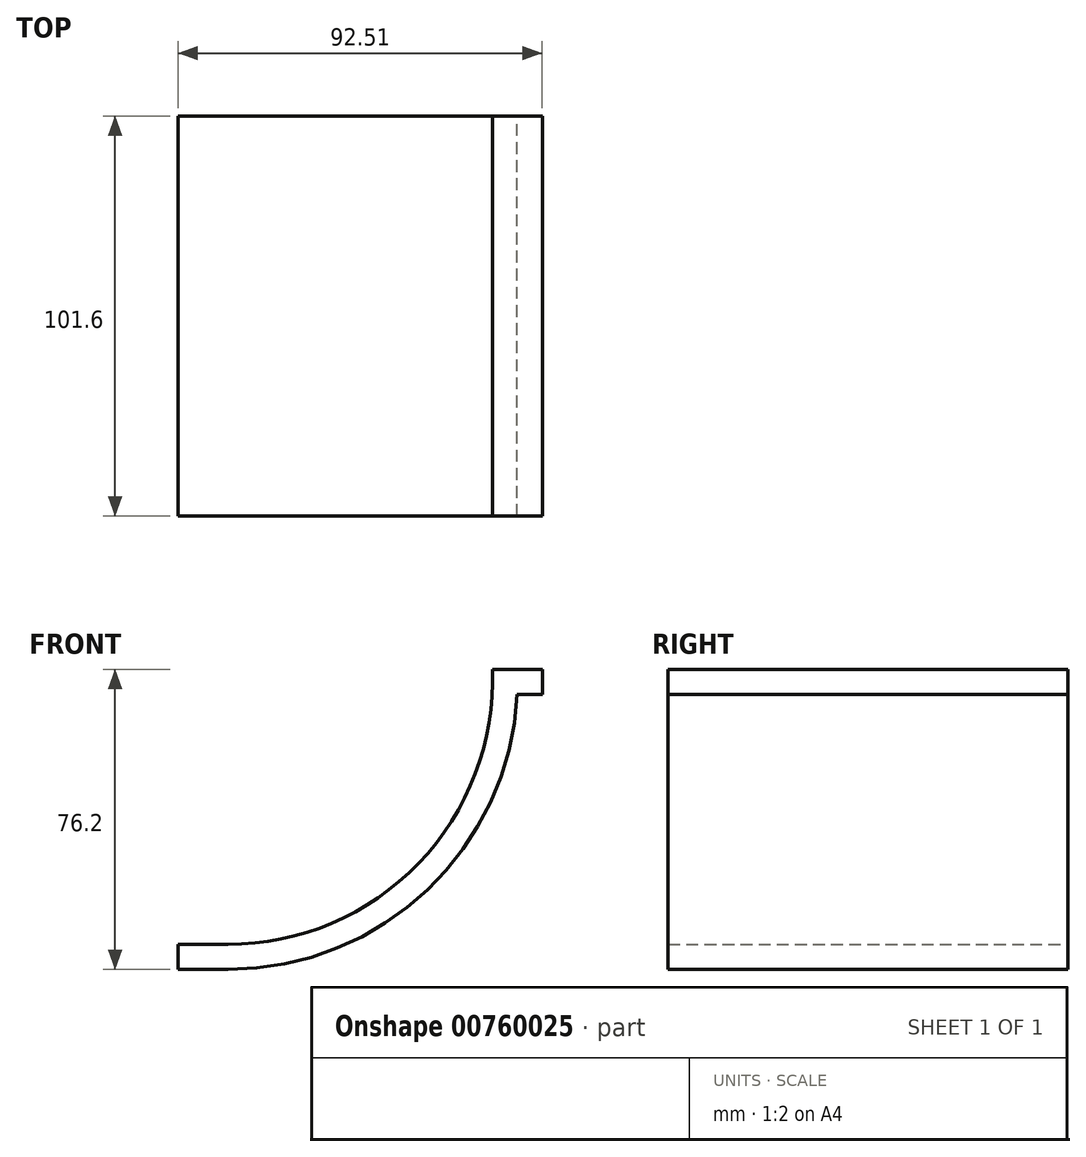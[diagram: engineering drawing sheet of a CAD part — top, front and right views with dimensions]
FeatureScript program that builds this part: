
annotation { "Feature Type Name" : "Feature", "Feature Type Description" : "" }
export const myFeature = defineFeature(function(context is Context, id is Id, definition is map)
    precondition{}
    {
        {
            var Q0;
            Q0=qCreatedBy(makeId("Front.planeOp"),FACE);
            var sketch = newSketch(context, id + "F0", { "sketchPlane" : qUnion([Q0])});
            skLineSegment(sketch, "E0.bottom", {"start": v(-65.8, -62.53) * mm, "end": v(-53.1, -62.53) * mm});
            skLineSegment(sketch, "E0.top", {"start": v(-65.8, -56.18) * mm, "end": v(-53.1, -56.18) * mm});
            skLineSegment(sketch, "E0.left", {"start": v(-65.8, -62.53) * mm, "end": v(-65.8, -56.18) * mm});
            skLineSegment(sketch, "E0.right", {"start": v(-53.1, -62.53) * mm, "end": v(-53.1, -56.18) * mm});
            skLineSegment(sketch, "E1.bottom", {"start": v(14.02, 7.32) * mm, "end": v(26.72, 7.32) * mm});
            skLineSegment(sketch, "E1.top", {"start": v(14.02, 13.67) * mm, "end": v(26.72, 13.67) * mm});
            skLineSegment(sketch, "E1.left", {"start": v(14.02, 7.32) * mm, "end": v(14.02, 13.67) * mm});
            skLineSegment(sketch, "E1.right", {"start": v(26.72, 7.32) * mm, "end": v(26.72, 13.67) * mm});
            skArc(sketch, "E2", {"start": v(-53.1, -56.18) * mm, "mid": v(-4.66, -35.55) * mm, "end": v(14.02, 13.67) * mm});
            skArc(sketch, "E3.0", {"start": v(-53.1, -62.53) * mm, "mid": v(-0.08, -39.95) * mm, "end": v(20.37, 13.92) * mm});
            skSolve(sketch);
        }
        {
            var Q0;
            {var subQ1=sQuery(id+"F0.wireOp",EDGE,"E0.right");Q0=makeQuery(id+"F0.imprint","IMPRINT",FACE,{"disambiguationData":[TD([[makeQuery(id+"F0.imprint","IMPRINT",EDGE,{"derivedFrom":subQ1}),-1.0]])]});}
            var Q1;
            {var subQ1=sQuery(id+"F0.wireOp",EDGE,"E1.left");var subQ5=sQuery(id+"F0.wireOp",EDGE,"E1.bottom");var subQ6=makeQuery(id+"F0.imprint","INTERSECT",VERTEX,{"derivedFrom":[subQ5,subQ1]});Q1=makeQuery(id+"F0.imprint","IMPRINT",FACE,{"disambiguationData":[TD([[makeQuery(id+"F0.imprint","IMPRINT",EDGE,{"disambiguationData":[TD([[subQ6,-1.0]])],"derivedFrom":subQ5}),1.0]])]});}
            var Q2;
            {var subQ0=sQuery(id+"F0.wireOp",EDGE,"E1.right");Q2=makeQuery(id+"F0.imprint","IMPRINT",FACE,{"disambiguationData":[TD([[makeQuery(id+"F0.imprint","IMPRINT",EDGE,{"derivedFrom":subQ0}),1.0]])]});}
            var Q3;
            Q3=makeQuery(id+"F0.imprint","IMPRINT",FACE,{"disambiguationData":[TD([[makeQuery(id+"F0.imprint","IMPRINT",EDGE,{"derivedFrom":sQuery(id+"F0.wireOp",EDGE,"E0.bottom")}),1.0]])]});
            extrude(context, id + "F1", {"entities" : qUnion([Q0, Q1, Q2, Q3]), "depth" : 101.6 * mm, "offsetDistance" : 25.4 * mm});
        }
    });
